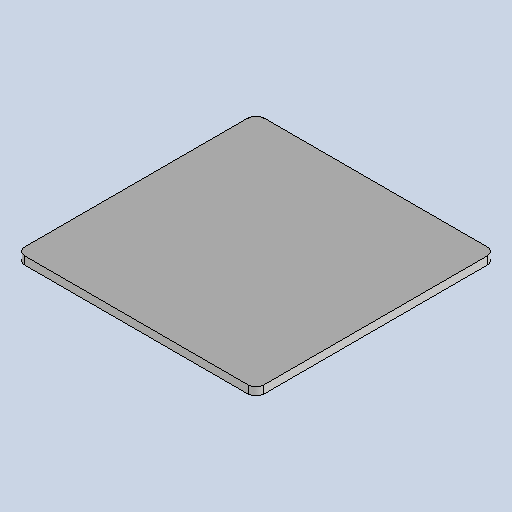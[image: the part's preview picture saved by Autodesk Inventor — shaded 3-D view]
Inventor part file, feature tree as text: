
AUTODESK INVENTOR PART (.ipt)
format: ipt  version: 2025.1 (Build 291241020, 241B)  size: 146,432 bytes
history: native  units: mm
features: other x2, sheet_metal_op x1, chamfer x1, sketch x1
ambient origin geometry x8: Origin, YZ Plane, XZ Plane, XY Plane, X Axis, Y Axis, Z Axis, Center Point
bodies: Body1 (feature_tree)
feature tree (5):
  sheet_metal_op  "Face3"
  chamfer  "Corner Round1"
  sketch  "Sketch1"  dims[d154=60.0mm d155=60.0mm d156=2.0mm d172=30.5mm d178=2.0mm]
  other  "Plate5"
  other  "Definition1"
